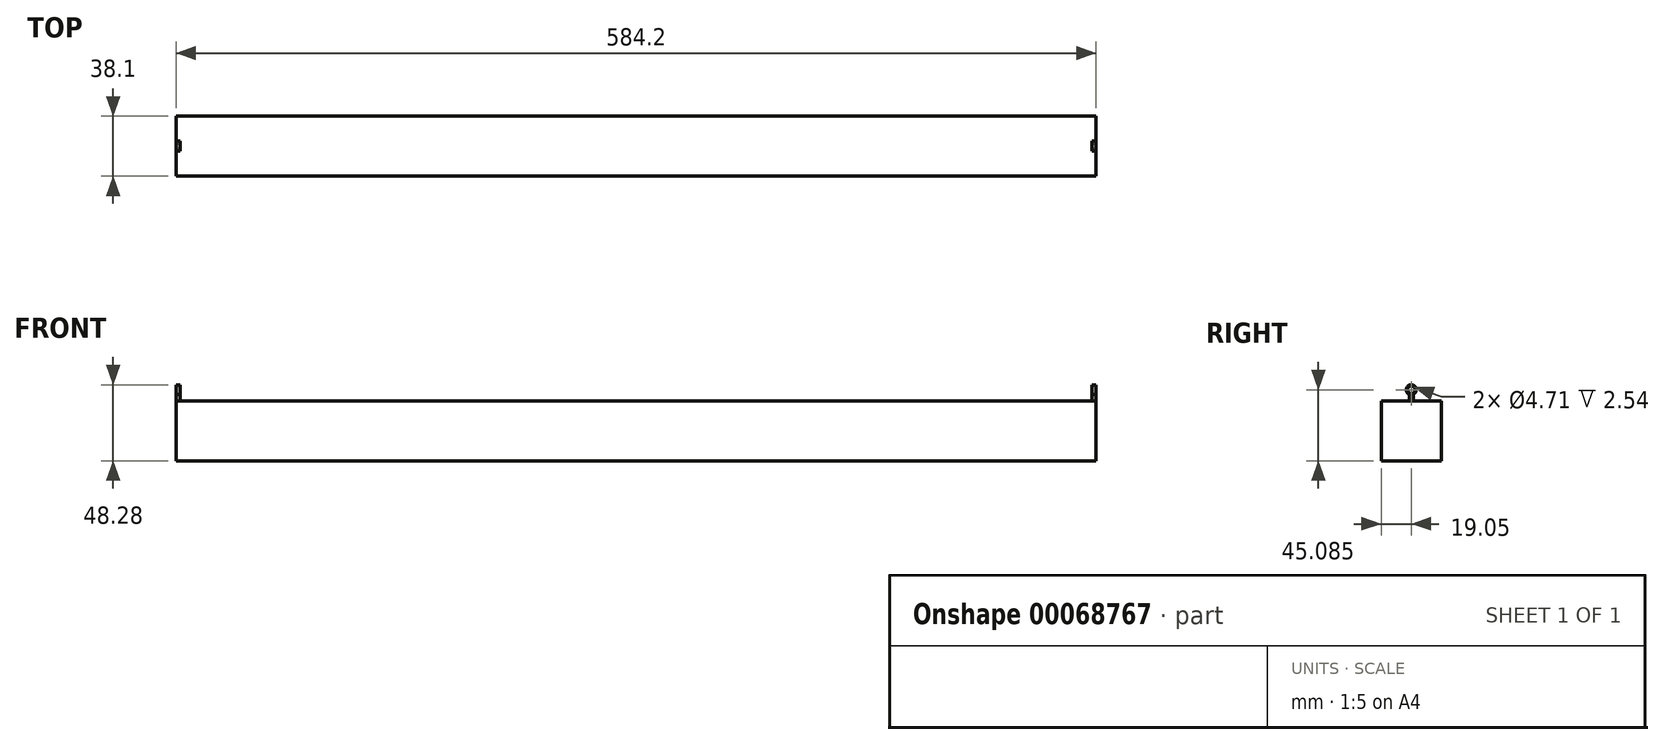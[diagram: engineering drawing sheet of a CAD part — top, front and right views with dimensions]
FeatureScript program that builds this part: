
annotation { "Feature Type Name" : "Feature", "Feature Type Description" : "" }
export const myFeature = defineFeature(function(context is Context, id is Id, definition is map)
    precondition{}
    {
        {
            var Q0;
            Q0=qCreatedBy(makeId("Top.planeOp"),FACE);
            var sketch = newSketch(context, id + "F0", { "sketchPlane" : qUnion([Q0])});
            skLineSegment(sketch, "E0.rect.bottom", {"start": v(292.1, 19.05) * mm, "end": v(-292.1, 19.05) * mm});
            skLineSegment(sketch, "E0.rect.top", {"start": v(292.1, -19.05) * mm, "end": v(-292.1, -19.05) * mm});
            skLineSegment(sketch, "E0.rect.left", {"start": v(292.1, 19.05) * mm, "end": v(292.1, -19.05) * mm});
            skLineSegment(sketch, "E0.rect.right", {"start": v(-292.1, 19.05) * mm, "end": v(-292.1, -19.05) * mm});
            skPoint(sketch, "E0.rect.middle", {"position": v(0, 0) * mm});
            skSolve(sketch);
        }
        {
            var Q0;
            Q0=makeQuery(id+"F0.imprint","IMPRINT",FACE,{"disambiguationData":[TD([[makeQuery(id+"F0.imprint","IMPRINT",EDGE,{"derivedFrom":sQuery(id+"F0.wireOp",EDGE,"E0.rect.bottom")}),1.0]])]});
            extrude(context, id + "F1", {"entities" : qUnion([Q0]), "depth" : 38.1 * mm});
        }
        {
            var Q0;
            Q0=makeQuery(id+"F1.opExtrude","SWEPT_FACE",FACE,{"disambiguationData":[OSD([sQuery(id+"F0.wireOp",EDGE,"E0.rect.left")])]});
            var sketch = newSketch(context, id + "F2", { "sketchPlane" : qUnion([Q0])});
            skLineSegment(sketch, "E1.rect.left", {"start": v(-1.27, 42.15) * mm, "end": v(-1.27, 38.1) * mm});
            skLineSegment(sketch, "E1.rect.right", {"start": v(1.27, 42.15) * mm, "end": v(1.27, 38.1) * mm});
            skLineSegment(sketch, "E2", {"start": v(1.27, 38.1) * mm, "end": v(-1.27, 38.1) * mm});
            skCircle(sketch, "E3", {"center": v(0, 45.09) * mm, "radius": 2.35 * mm});
            skArc(sketch, "E4", {"start": v(1.27, 42.15) * mm, "mid": v(0, 48.28) * mm, "end": v(-1.27, 42.15) * mm});
            skSolve(sketch);
        }
        {
            var Q0;
            Q0=makeQuery(id+"F2.imprint","IMPRINT",FACE,{"disambiguationData":[TD([[makeQuery(id+"F2.imprint","IMPRINT",EDGE,{"derivedFrom":sQuery(id+"F2.wireOp",EDGE,"E1.rect.left")}),1.0]])]});
            extrude(context, id + "F3", {"entities" : qUnion([Q0]), "oppositeDirection" : true, "depth" : 2.54 * mm});
        }
        {
            var Q0;
            Q0=makeQuery(id+"F3.opExtrude","CAP_FACE",FACE,{"disambiguationData":[OSD([sQuery(id+"F2.wireOp",EDGE,"E1.rect.left"),sQuery(id+"F2.wireOp",EDGE,"E1.rect.right"),sQuery(id+"F2.wireOp",EDGE,"E2"),sQuery(id+"F2.wireOp",EDGE,"E3"),sQuery(id+"F2.wireOp",EDGE,"E4")])],"isStart":true});
            extrude(context, id + "F4", {"entities" : qUnion([Q0]), "operationType" : NewBodyOperationType.ADD, "oppositeDirection" : true, "depth" : 584.2 * mm, "hasSecondDirection" : true, "secondDirectionOppositeDirection" : true, "secondDirectionDepth" : 581.66 * mm});
        }
    });
